# Revit family: P200921MX-006c_MDB9959SKZ
name_source: partatom
category: Specialty Equipment
units: mm (PartAtom-declared; Revit-internal decimal feet)

## family parameters
Always vertical = Yes
Cut with Voids When Loaded = No
Enable Cutting in Views = No
Maintain Annotation Orientation = No
Part Type = Normal
Room Calculation Point = No
Round Connector Dimension = Use Diameter
Shared = No
Work Plane-Based = No

## types (1)
- MDB9959SKZ
    Accent Material = ARCAT - Metal - Steel - Black
    Amps = 0 A
    Base Fitting Material = ARCAT - Metal - Plastic - Cream
    Blanket Material = ARCAT - Fabric - Grey
    Body Material = ARCAT - Metal - Plastic - Grey
    Bottom Panel Material = ARCAT - Metal - Steel - Black
    Clearance Material = ARCAT - Clearance
    Default Elevation = 0"
    Depth = 24 1/2"
    Description = Top control dishwasher with Third Level Rack and Dual Power filtration
Lave-vaisselle à panier de troisième niveau et filtration à puissance double
    Dimension Guide = https://www.whirlpool.com
https://www.whirlpool.com
    Display Panel Material = ARCAT - Glass - Black
    Door Material = ARCAT - Metal - Steel - Stainless
    Energy Guide = https://www.whirlpool.com
https://www.whirlpool.com
    Family Name = Cleaning
    Feature 1 = Dual Power Filtration
Filtration à puissance double
    Feature 2 = Steam Sanitize option
Option d'assainissement à la vapeur
    Feature 3 = 3rd Level Rack
Panier de 3ᵉ niveau
    Handle Material = ARCAT - Metal - Steel - Stainless
    Height = 34 1/2"
    Manufacturer = Maytag
    Model = MDB9959SKZ
    Voltage = 0 V
    Width = 23 7/8"

## geometry (parser evidence)
native form markers: Sweep x4
no freeform markers — native parametric forms only
